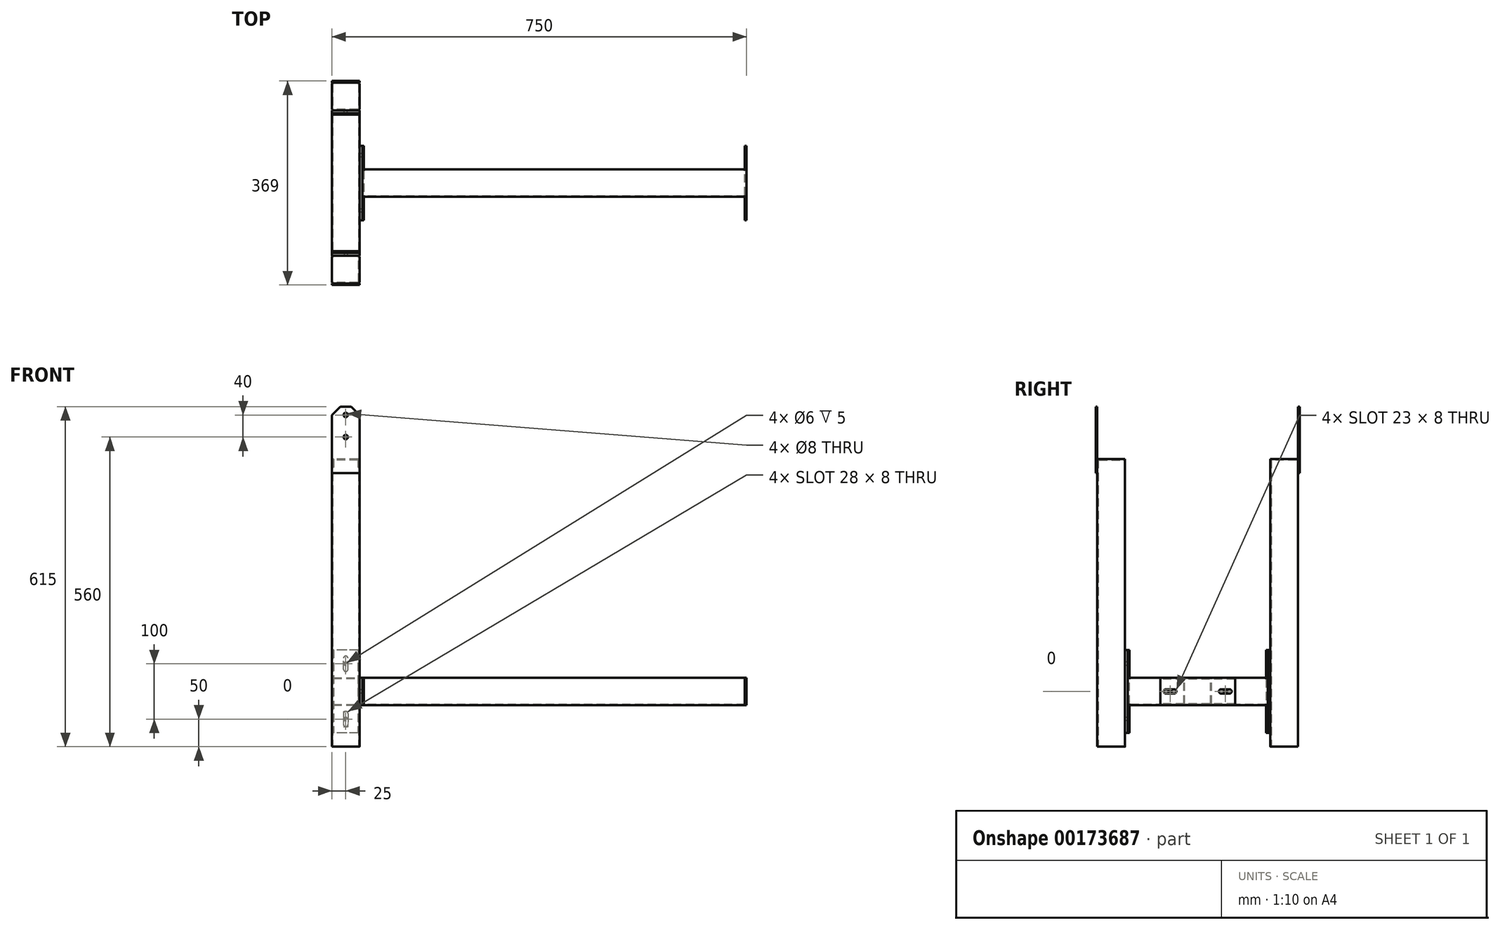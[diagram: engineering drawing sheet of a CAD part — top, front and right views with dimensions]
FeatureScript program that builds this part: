
annotation { "Feature Type Name" : "Feature", "Feature Type Description" : "" }
export const myFeature = defineFeature(function(context is Context, id is Id, definition is map)
    precondition{}
    {
        {
            var Q0;
            Q0=qCreatedBy(makeId("Top.planeOp"),FACE);
            var sketch = newSketch(context, id + "F0", { "sketchPlane" : qUnion([Q0])});
            skLineSegment(sketch, "E0.bottom", {"start": v(22, -25) * mm, "end": v(-22, -25) * mm});
            skLineSegment(sketch, "E0.top", {"start": v(22, 25) * mm, "end": v(-22, 25) * mm});
            skLineSegment(sketch, "E0.left", {"start": v(25, -22) * mm, "end": v(25, 22) * mm});
            skLineSegment(sketch, "E0.right", {"start": v(-25, -22) * mm, "end": v(-25, 22) * mm});
            skPoint(sketch, "E0.middle", {"position": v(0, 0) * mm});
            skPoint(sketch, "E1.visualSharp", {"position": v(-25, 25) * mm});
            skArc(sketch, "E1.filletArc", {"start": v(-22, 25) * mm, "mid": v(-24.12, 24.12) * mm, "end": v(-25, 22) * mm});
            skPoint(sketch, "E2.visualSharp", {"position": v(25, 25) * mm});
            skArc(sketch, "E2.filletArc", {"start": v(25, 22) * mm, "mid": v(24.12, 24.12) * mm, "end": v(22, 25) * mm});
            skPoint(sketch, "E3.visualSharp", {"position": v(25, -25) * mm});
            skArc(sketch, "E3.filletArc", {"start": v(22, -25) * mm, "mid": v(24.12, -24.12) * mm, "end": v(25, -22) * mm});
            skPoint(sketch, "E4.visualSharp", {"position": v(-25, -25) * mm});
            skArc(sketch, "E4.filletArc", {"start": v(-25, -22) * mm, "mid": v(-24.12, -24.12) * mm, "end": v(-22, -25) * mm});
            skArc(sketch, "E5.0", {"start": v(23.5, 22) * mm, "mid": v(23.06, 23.06) * mm, "end": v(22, 23.5) * mm});
            skLineSegment(sketch, "E5.1", {"start": v(23.5, -22) * mm, "end": v(23.5, 22) * mm});
            skLineSegment(sketch, "E5.2", {"start": v(22, 23.5) * mm, "end": v(-22, 23.5) * mm});
            skArc(sketch, "E5.3", {"start": v(22, -23.5) * mm, "mid": v(23.06, -23.06) * mm, "end": v(23.5, -22) * mm});
            skArc(sketch, "E5.4", {"start": v(-22, 23.5) * mm, "mid": v(-23.06, 23.06) * mm, "end": v(-23.5, 22) * mm});
            skLineSegment(sketch, "E5.5", {"start": v(-23.5, -22) * mm, "end": v(-23.5, 22) * mm});
            skArc(sketch, "E5.6", {"start": v(-23.5, -22) * mm, "mid": v(-23.06, -23.06) * mm, "end": v(-22, -23.5) * mm});
            skLineSegment(sketch, "E5.7", {"start": v(22, -23.5) * mm, "end": v(-22, -23.5) * mm});
            skSolve(sketch);
        }
        {
            var Q0;
            Q0=makeQuery(id+"F0.imprint","IMPRINT",FACE,{"disambiguationData":[TD([[makeQuery(id+"F0.imprint","IMPRINT",EDGE,{"derivedFrom":sQuery(id+"F0.wireOp",EDGE,"E0.bottom")}),-1.0]])]});
            extrude(context, id + "F1", {"entities" : qUnion([Q0]), "depth" : 520 * mm});
        }
        {
            var Q0;
            Q0=makeQuery(id+"F1.opExtrude","SWEPT_FACE",FACE,{"disambiguationData":[OSD([sQuery(id+"F0.wireOp",EDGE,"E0.top")])]});
            var sketch = newSketch(context, id + "F2", { "sketchPlane" : qUnion([Q0])});
            skLineSegment(sketch, "E6.bottom", {"start": v(-25, 175) * mm, "end": v(25, 175) * mm});
            skLineSegment(sketch, "E6.top", {"start": v(-25, 25) * mm, "end": v(25, 25) * mm});
            skLineSegment(sketch, "E6.left", {"start": v(-25, 175) * mm, "end": v(-25, 25) * mm});
            skLineSegment(sketch, "E6.right", {"start": v(25, 175) * mm, "end": v(25, 25) * mm});
            skCircle(sketch, "E7", {"center": v(0, 150) * mm, "radius": 3 * mm});
            skCircle(sketch, "E8", {"center": v(0, 50) * mm, "radius": 3 * mm});
            skLineSegment(sketch, "E9", {"start": v(25, 100) * mm, "end": v(-25, 100) * mm, "construction": true});
            skPoint(sketch, "E10.middle", {"position": v(0, 100) * mm});
            skLineSegment(sketch, "E11", {"start": v(0, 125) * mm, "end": v(0, 75) * mm, "construction": true});
            skLineSegment(sketch, "E12", {"start": v(-89.65, -125) * mm, "end": v(137.55, -125) * mm, "construction": true});
            skSolve(sketch);
        }
        {
            var Q0;
            Q0=qSketchRegion(id+"F2",true);
            extrude(context, id + "F3", {"entities" : qUnion([Q0]), "operationType" : NewBodyOperationType.ADD, "depth" : 5 * mm});
        }
        {
            var Q0;
            Q0=makeQuery(id+"F1.opExtrude","CAP_FACE",FACE,{"disambiguationData":[OSD([sQuery(id+"F0.wireOp",EDGE,"E0.bottom"),sQuery(id+"F0.wireOp",EDGE,"E0.top"),sQuery(id+"F0.wireOp",EDGE,"E0.left"),sQuery(id+"F0.wireOp",EDGE,"E0.right"),sQuery(id+"F0.wireOp",EDGE,"E1.filletArc"),sQuery(id+"F0.wireOp",EDGE,"E2.filletArc"),sQuery(id+"F0.wireOp",EDGE,"E3.filletArc"),sQuery(id+"F0.wireOp",EDGE,"E4.filletArc"),sQuery(id+"F0.wireOp",EDGE,"E5.0"),sQuery(id+"F0.wireOp",EDGE,"E5.1"),sQuery(id+"F0.wireOp",EDGE,"E5.2"),sQuery(id+"F0.wireOp",EDGE,"E5.3"),sQuery(id+"F0.wireOp",EDGE,"E5.4"),sQuery(id+"F0.wireOp",EDGE,"E5.5"),sQuery(id+"F0.wireOp",EDGE,"E5.6"),sQuery(id+"F0.wireOp",EDGE,"E5.7")])],"isStart":false});
            var sketch = newSketch(context, id + "F4", { "sketchPlane" : qUnion([Q0])});
            skLineSegment(sketch, "E13.0", {"start": v(-25, -22) * mm, "end": v(-25, 22) * mm});
            skArc(sketch, "E13.1", {"start": v(-25, -22) * mm, "mid": v(-24.12, -24.12) * mm, "end": v(-22, -25) * mm});
            skLineSegment(sketch, "E13.2", {"start": v(22, -25) * mm, "end": v(-22, -25) * mm});
            skArc(sketch, "E13.3", {"start": v(22, -25) * mm, "mid": v(24.12, -24.12) * mm, "end": v(25, -22) * mm});
            skLineSegment(sketch, "E13.4", {"start": v(25, -22) * mm, "end": v(25, 22) * mm});
            skArc(sketch, "E13.5", {"start": v(25, 22) * mm, "mid": v(24.12, 24.12) * mm, "end": v(22, 25) * mm});
            skLineSegment(sketch, "E13.6", {"start": v(22, 25) * mm, "end": v(-22, 25) * mm});
            skArc(sketch, "E13.7", {"start": v(-22, 25) * mm, "mid": v(-24.12, 24.12) * mm, "end": v(-25, 22) * mm});
            skSolve(sketch);
        }
        {
            var Q0;
            Q0=makeQuery(id+"F4.imprint","IMPRINT",FACE,{"disambiguationData":[TD([[makeQuery(id+"F4.imprint","IMPRINT",EDGE,{"derivedFrom":makeQuery(id+"F1.opExtrude","CAP_EDGE",EDGE,{"disambiguationData":[OSD([sQuery(id+"F0.wireOp",EDGE,"E5.0")])],"isStart":false})}),1.0]])]});
            extrude(context, id + "F5", {"entities" : qUnion([Q0]), "operationType" : NewBodyOperationType.ADD, "oppositeDirection" : true, "depth" : 1.5 * mm});
        }
        {
            var Q0;
            Q0=makeQuery(id+"F1.opExtrude","SWEPT_FACE",FACE,{"disambiguationData":[OSD([sQuery(id+"F0.wireOp",EDGE,"E0.bottom")])]});
            var sketch = newSketch(context, id + "F6", { "sketchPlane" : qUnion([Q0])});
            skLineSegment(sketch, "E14.bottom", {"start": v(-25, 615) * mm, "end": v(25, 615) * mm});
            skLineSegment(sketch, "E14.top", {"start": v(-25, 495) * mm, "end": v(25, 495) * mm});
            skLineSegment(sketch, "E14.left", {"start": v(-25, 615) * mm, "end": v(-25, 495) * mm});
            skLineSegment(sketch, "E14.right", {"start": v(25, 615) * mm, "end": v(25, 495) * mm});
            skCircle(sketch, "E15", {"center": v(0, 600) * mm, "radius": 4 * mm});
            skCircle(sketch, "E16", {"center": v(0, 560) * mm, "radius": 4 * mm});
            skSolve(sketch);
        }
        {
            var Q0;
            Q0=qSketchRegion(id+"F6",true);
            extrude(context, id + "F7", {"entities" : qUnion([Q0]), "operationType" : NewBodyOperationType.ADD, "depth" : 3 * mm});
        }
        {
            var Q0;
            Q0=makeQuery(id+"F7.opExtrude","SWEPT_EDGE",EDGE,{"disambiguationData":[OSD([sQuery(id+"F6.wireOp",EDGE,"E14.bottom"),sQuery(id+"F6.wireOp",EDGE,"E14.right")])]});
            var Q1;
            Q1=makeQuery(id+"F7.opExtrude","SWEPT_EDGE",EDGE,{"disambiguationData":[OSD([sQuery(id+"F6.wireOp",EDGE,"E14.bottom"),sQuery(id+"F6.wireOp",EDGE,"E14.left")])]});
            chamfer(context, id + "F8", {"entities" : qUnion([Q0, Q1]), "width" : 15 * mm, "tangentPropagation" : true});
        }
        {
            var Q0;
            Q0=makeQuery(id+"F7.opExtrude","CAP_FACE",FACE,{"disambiguationData":[OSD([sQuery(id+"F6.wireOp",EDGE,"E14.bottom"),sQuery(id+"F6.wireOp",EDGE,"E14.top"),sQuery(id+"F6.wireOp",EDGE,"E14.left"),sQuery(id+"F6.wireOp",EDGE,"E14.right"),sQuery(id+"F6.wireOp",EDGE,"E15"),sQuery(id+"F6.wireOp",EDGE,"E16")])],"isStart":true});
            cPlane(context, id + "F9", {"entities" : qUnion([Q0]), "cplaneType" : CPlaneType.OFFSET, "offset" : (363 / 2) * mm, "width" : 150 * mm, "height" : 150 * mm});
        }
        {
            var Q0;
            Q0=makeQuery(id+"F1.opExtrude","SWEPT_BODY",BODY,{"disambiguationData":[OSD([sQuery(id+"F0.wireOp",EDGE,"E0.bottom"),sQuery(id+"F0.wireOp",EDGE,"E0.top"),sQuery(id+"F0.wireOp",EDGE,"E0.left"),sQuery(id+"F0.wireOp",EDGE,"E0.right"),sQuery(id+"F0.wireOp",EDGE,"E1.filletArc"),sQuery(id+"F0.wireOp",EDGE,"E2.filletArc"),sQuery(id+"F0.wireOp",EDGE,"E3.filletArc"),sQuery(id+"F0.wireOp",EDGE,"E4.filletArc"),sQuery(id+"F0.wireOp",EDGE,"E5.0"),sQuery(id+"F0.wireOp",EDGE,"E5.1"),sQuery(id+"F0.wireOp",EDGE,"E5.2"),sQuery(id+"F0.wireOp",EDGE,"E5.3"),sQuery(id+"F0.wireOp",EDGE,"E5.4"),sQuery(id+"F0.wireOp",EDGE,"E5.5"),sQuery(id+"F0.wireOp",EDGE,"E5.6"),sQuery(id+"F0.wireOp",EDGE,"E5.7")])]});
            var Q1;
            Q1=qCreatedBy(id+"F9.planeOp",FACE);
            mirror(context, id + "F10", {"entities" : qUnion([Q0]), "mirrorPlane" : qUnion([Q1])});
        }
        {
            var Q0;
            Q0=makeQuery(id+"F3.opExtrude","CAP_FACE",FACE,{"disambiguationData":[OSD([sQuery(id+"F2.wireOp",EDGE,"E6.bottom"),sQuery(id+"F2.wireOp",EDGE,"E6.top"),sQuery(id+"F2.wireOp",EDGE,"E6.left"),sQuery(id+"F2.wireOp",EDGE,"E6.right"),sQuery(id+"F2.wireOp",EDGE,"E7"),sQuery(id+"F2.wireOp",EDGE,"E8")])],"isStart":false});
            var sketch = newSketch(context, id + "F11", { "sketchPlane" : qUnion([Q0])});
            skLineSegment(sketch, "E17.0", {"start": v(-25, 175) * mm, "end": v(25, 175) * mm});
            skLineSegment(sketch, "E17.1", {"start": v(25, 175) * mm, "end": v(25, 25) * mm});
            skLineSegment(sketch, "E17.2", {"start": v(-25, 175) * mm, "end": v(-25, 25) * mm});
            skLineSegment(sketch, "E17.3", {"start": v(-25, 25) * mm, "end": v(25, 25) * mm});
            skCircle(sketch, "E18.0", {"center": v(0, 150) * mm, "radius": 3 * mm, "construction": true});
            skCircle(sketch, "E18.1", {"center": v(0, 50) * mm, "radius": 3 * mm, "construction": true});
            skLineSegment(sketch, "E19.bottom", {"start": v(4, 140) * mm, "end": v(-4, 140) * mm, "construction": true});
            skLineSegment(sketch, "E19.top", {"start": v(4, 160) * mm, "end": v(-4, 160) * mm, "construction": true});
            skLineSegment(sketch, "E19.left", {"start": v(4, 140) * mm, "end": v(4, 160) * mm});
            skLineSegment(sketch, "E19.right", {"start": v(-4, 140) * mm, "end": v(-4, 160) * mm});
            skLineSegment(sketch, "E20.bottom", {"start": v(-4, 60) * mm, "end": v(4, 60) * mm, "construction": true});
            skLineSegment(sketch, "E20.top", {"start": v(-4, 40) * mm, "end": v(4, 40) * mm, "construction": true});
            skLineSegment(sketch, "E20.left", {"start": v(-4, 60) * mm, "end": v(-4, 40) * mm});
            skLineSegment(sketch, "E20.right", {"start": v(4, 60) * mm, "end": v(4, 40) * mm});
            skArc(sketch, "E21", {"start": v(4, 160) * mm, "mid": v(0, 164) * mm, "end": v(-4, 160) * mm});
            skArc(sketch, "E22", {"start": v(-4, 140) * mm, "mid": v(0, 136) * mm, "end": v(4, 140) * mm});
            skArc(sketch, "E23", {"start": v(4, 60) * mm, "mid": v(0, 64) * mm, "end": v(-4, 60) * mm});
            skArc(sketch, "E24", {"start": v(-4, 40) * mm, "mid": v(0, 36) * mm, "end": v(4, 40) * mm});
            skSolve(sketch);
        }
        {
            var Q0;
            Q0=qSketchRegion(id+"F11",true);
            extrude(context, id + "F12", {"entities" : qUnion([Q0]), "depth" : 3 * mm});
        }
        {
            var Q0;
            Q0=makeQuery(id+"F12.opExtrude","SWEPT_BODY",BODY,{"disambiguationData":[OSD([sQuery(id+"F11.wireOp",EDGE,"E17.0"),sQuery(id+"F11.wireOp",EDGE,"E17.1"),sQuery(id+"F11.wireOp",EDGE,"E17.2"),sQuery(id+"F11.wireOp",EDGE,"E17.3"),sQuery(id+"F11.wireOp",EDGE,"E19.left"),sQuery(id+"F11.wireOp",EDGE,"E19.right"),sQuery(id+"F11.wireOp",EDGE,"E20.left"),sQuery(id+"F11.wireOp",EDGE,"E20.right"),sQuery(id+"F11.wireOp",EDGE,"E21"),sQuery(id+"F11.wireOp",EDGE,"E22"),sQuery(id+"F11.wireOp",EDGE,"E23"),sQuery(id+"F11.wireOp",EDGE,"E24")])]});
            var Q1;
            Q1=qCreatedBy(id+"F9.planeOp",FACE);
            mirror(context, id + "F13", {"entities" : qUnion([Q0]), "mirrorPlane" : qUnion([Q1])});
        }
        {
            var Q0;
            Q0=makeQuery(id+"F12.opExtrude","CAP_FACE",FACE,{"disambiguationData":[OSD([sQuery(id+"F11.wireOp",EDGE,"E17.0"),sQuery(id+"F11.wireOp",EDGE,"E17.1"),sQuery(id+"F11.wireOp",EDGE,"E17.2"),sQuery(id+"F11.wireOp",EDGE,"E17.3"),sQuery(id+"F11.wireOp",EDGE,"E19.left"),sQuery(id+"F11.wireOp",EDGE,"E19.right"),sQuery(id+"F11.wireOp",EDGE,"E20.left"),sQuery(id+"F11.wireOp",EDGE,"E20.right"),sQuery(id+"F11.wireOp",EDGE,"E21"),sQuery(id+"F11.wireOp",EDGE,"E22"),sQuery(id+"F11.wireOp",EDGE,"E23"),sQuery(id+"F11.wireOp",EDGE,"E24")])],"isStart":false});
            var sketch = newSketch(context, id + "F14", { "sketchPlane" : qUnion([Q0])});
            skLineSegment(sketch, "E25", {"start": v(-25, 100) * mm, "end": v(25, 100) * mm, "construction": true});
            skLineSegment(sketch, "E26.bottom", {"start": v(22, 75) * mm, "end": v(-22, 75) * mm});
            skLineSegment(sketch, "E26.top", {"start": v(22, 125) * mm, "end": v(-22, 125) * mm});
            skLineSegment(sketch, "E26.left", {"start": v(25, 78) * mm, "end": v(25, 122) * mm});
            skLineSegment(sketch, "E26.right", {"start": v(-25, 78) * mm, "end": v(-25, 122) * mm});
            skPoint(sketch, "E26.middle", {"position": v(0, 100) * mm});
            skPoint(sketch, "E27.visualSharp", {"position": v(-25, 125) * mm});
            skArc(sketch, "E27.filletArc", {"start": v(-22, 125) * mm, "mid": v(-24.12, 124.12) * mm, "end": v(-25, 122) * mm});
            skPoint(sketch, "E28.visualSharp", {"position": v(25, 125) * mm});
            skArc(sketch, "E28.filletArc", {"start": v(25, 122) * mm, "mid": v(24.12, 124.12) * mm, "end": v(22, 125) * mm});
            skPoint(sketch, "E29.visualSharp", {"position": v(25, 75) * mm});
            skArc(sketch, "E29.filletArc", {"start": v(22, 75) * mm, "mid": v(24.12, 75.88) * mm, "end": v(25, 78) * mm});
            skPoint(sketch, "E30.visualSharp", {"position": v(-25, 75) * mm});
            skArc(sketch, "E30.filletArc", {"start": v(-25, 78) * mm, "mid": v(-24.12, 75.88) * mm, "end": v(-22, 75) * mm});
            skArc(sketch, "E31.0", {"start": v(23.5, 122) * mm, "mid": v(23.06, 123.06) * mm, "end": v(22, 123.5) * mm});
            skLineSegment(sketch, "E31.1", {"start": v(23.5, 78) * mm, "end": v(23.5, 122) * mm});
            skLineSegment(sketch, "E31.2", {"start": v(22, 123.5) * mm, "end": v(-22, 123.5) * mm});
            skArc(sketch, "E31.3", {"start": v(22, 76.5) * mm, "mid": v(23.06, 76.94) * mm, "end": v(23.5, 78) * mm});
            skArc(sketch, "E31.4", {"start": v(-22, 123.5) * mm, "mid": v(-23.06, 123.06) * mm, "end": v(-23.5, 122) * mm});
            skLineSegment(sketch, "E31.5", {"start": v(-23.5, 78) * mm, "end": v(-23.5, 122) * mm});
            skArc(sketch, "E31.6", {"start": v(-23.5, 78) * mm, "mid": v(-23.06, 76.94) * mm, "end": v(-22, 76.5) * mm});
            skLineSegment(sketch, "E31.7", {"start": v(22, 76.5) * mm, "end": v(-22, 76.5) * mm});
            skSolve(sketch);
        }
        {
            var Q0;
            Q0=qSketchRegion(id+"F14",true);
            extrude(context, id + "F15", {"entities" : qUnion([Q0]), "operationType" : NewBodyOperationType.ADD, "endBound" : BoundingType.UP_TO_NEXT, "depth" : 25 * mm});
        }
        {
            var Q0;
            Q0=makeQuery(id+"F1.opExtrude","SWEPT_FACE",FACE,{"disambiguationData":[OSD([sQuery(id+"F0.wireOp",EDGE,"E0.left")])]});
            cPlane(context, id + "F16", {"entities" : qUnion([Q0]), "cplaneType" : CPlaneType.OFFSET, "offset" : 352.5 * mm, "width" : 150 * mm, "height" : 150 * mm});
        }
        {
            var Q0;
            {var subQ0=makeQuery(id+"F12.opExtrude","SWEPT_FACE",FACE,{"disambiguationData":[OSD([sQuery(id+"F11.wireOp",EDGE,"E17.2")])]});Q0=makeQuery(id+"F15.boolean.opBoolean","MERGE",FACE,{"derivedFrom":[subQ0,makeQuery(id+"F13.opPattern","COPY",FACE,{"derivedFrom":subQ0,"instanceName":"1"}),makeQuery(id+"F15.opExtrude","SWEPT_FACE",FACE,{"disambiguationData":[OSD([sQuery(id+"F14.wireOp",EDGE,"E26.right")])]})]});}
            var sketch = newSketch(context, id + "F17", { "sketchPlane" : qUnion([Q0])});
            skLineSegment(sketch, "E32.bottom", {"start": v(89, 125) * mm, "end": v(224, 125) * mm});
            skLineSegment(sketch, "E32.top", {"start": v(89, 75) * mm, "end": v(224, 75) * mm});
            skLineSegment(sketch, "E32.left", {"start": v(89, 125) * mm, "end": v(89, 75) * mm});
            skLineSegment(sketch, "E32.right", {"start": v(224, 125) * mm, "end": v(224, 75) * mm});
            skLineSegment(sketch, "E33", {"start": v(224, 100) * mm, "end": v(89, 100) * mm, "construction": true});
            skPoint(sketch, "E34.middle", {"position": v(156.5, 100) * mm});
            skLineSegment(sketch, "E35", {"start": v(156.5, 122) * mm, "end": v(156.5, 78) * mm, "construction": true});
            skCircle(sketch, "E36", {"center": v(106.5, 100) * mm, "radius": 3 * mm});
            skCircle(sketch, "E37.MirrorC", {"center": v(206.5, 100) * mm, "radius": 3 * mm});
            skSolve(sketch);
        }
        {
            var Q0;
            Q0=qSketchRegion(id+"F17",true);
            extrude(context, id + "F18", {"entities" : qUnion([Q0]), "operationType" : NewBodyOperationType.ADD, "depth" : 5 * mm});
        }
        {
            var Q0;
            Q0=makeQuery(id+"F18.opExtrude","CAP_FACE",FACE,{"disambiguationData":[OSD([sQuery(id+"F17.wireOp",EDGE,"E32.bottom"),sQuery(id+"F17.wireOp",EDGE,"E32.top"),sQuery(id+"F17.wireOp",EDGE,"E32.left"),sQuery(id+"F17.wireOp",EDGE,"E32.right"),sQuery(id+"F17.wireOp",EDGE,"E36"),sQuery(id+"F17.wireOp",EDGE,"E37.MirrorC")])],"isStart":false});
            var sketch = newSketch(context, id + "F19", { "sketchPlane" : qUnion([Q0])});
            skLineSegment(sketch, "E38.0", {"start": v(89, 125) * mm, "end": v(224, 125) * mm});
            skLineSegment(sketch, "E38.1", {"start": v(89, 125) * mm, "end": v(89, 75) * mm});
            skLineSegment(sketch, "E38.2", {"start": v(89, 75) * mm, "end": v(224, 75) * mm});
            skLineSegment(sketch, "E38.3", {"start": v(224, 125) * mm, "end": v(224, 75) * mm});
            skCircle(sketch, "E38.4", {"center": v(206.5, 100) * mm, "radius": 3 * mm, "construction": true});
            skCircle(sketch, "E38.5", {"center": v(106.5, 100) * mm, "radius": 3 * mm, "construction": true});
            skCircle(sketch, "E39", {"center": v(106.5, 100) * mm, "radius": 4 * mm});
            skCircle(sketch, "E40", {"center": v(206.5, 100) * mm, "radius": 4 * mm});
            skSolve(sketch);
        }
        {
            var Q0;
            Q0=qSketchRegion(id+"F19",true);
            extrude(context, id + "F20", {"entities" : qUnion([Q0]), "depth" : 3 * mm});
        }
        {
            var Q0;
            Q0=makeQuery(id+"F20.opExtrude","SWEPT_BODY",BODY,{"disambiguationData":[OSD([sQuery(id+"F19.wireOp",EDGE,"E38.0"),sQuery(id+"F19.wireOp",EDGE,"E38.1"),sQuery(id+"F19.wireOp",EDGE,"E38.2"),sQuery(id+"F19.wireOp",EDGE,"E38.3"),sQuery(id+"F19.wireOp",EDGE,"E39"),sQuery(id+"F19.wireOp",EDGE,"E40")])]});
            var Q1;
            Q1=qCreatedBy(id+"F16.planeOp",FACE);
            mirror(context, id + "F21", {"entities" : qUnion([Q0]), "mirrorPlane" : qUnion([Q1])});
        }
        {
            var Q0;
            Q0=makeQuery(id+"F20.opExtrude","CAP_FACE",FACE,{"disambiguationData":[OSD([sQuery(id+"F19.wireOp",EDGE,"E38.0"),sQuery(id+"F19.wireOp",EDGE,"E38.1"),sQuery(id+"F19.wireOp",EDGE,"E38.2"),sQuery(id+"F19.wireOp",EDGE,"E38.3"),sQuery(id+"F19.wireOp",EDGE,"E39"),sQuery(id+"F19.wireOp",EDGE,"E40")])],"isStart":false});
            var sketch = newSketch(context, id + "F22", { "sketchPlane" : qUnion([Q0])});
            skLineSegment(sketch, "E41", {"start": v(139.88, 100) * mm, "end": v(173.12, 100) * mm, "construction": true});
            skLineSegment(sketch, "E42.bottom", {"start": v(178.5, 75) * mm, "end": v(134.5, 75) * mm});
            skLineSegment(sketch, "E42.top", {"start": v(178.5, 125) * mm, "end": v(134.5, 125) * mm});
            skLineSegment(sketch, "E42.left", {"start": v(181.5, 78) * mm, "end": v(181.5, 122) * mm});
            skLineSegment(sketch, "E42.right", {"start": v(131.5, 78) * mm, "end": v(131.5, 122) * mm});
            skPoint(sketch, "E42.middle", {"position": v(156.5, 100) * mm});
            skPoint(sketch, "E43.visualSharp", {"position": v(131.5, 125) * mm});
            skArc(sketch, "E43.filletArc", {"start": v(134.5, 125) * mm, "mid": v(132.38, 124.12) * mm, "end": v(131.5, 122) * mm});
            skPoint(sketch, "E44.visualSharp", {"position": v(181.5, 125) * mm});
            skArc(sketch, "E44.filletArc", {"start": v(181.5, 122) * mm, "mid": v(180.62, 124.12) * mm, "end": v(178.5, 125) * mm});
            skPoint(sketch, "E45.visualSharp", {"position": v(181.5, 75) * mm});
            skArc(sketch, "E45.filletArc", {"start": v(178.5, 75) * mm, "mid": v(180.62, 75.88) * mm, "end": v(181.5, 78) * mm});
            skPoint(sketch, "E46.visualSharp", {"position": v(131.5, 75) * mm});
            skArc(sketch, "E46.filletArc", {"start": v(131.5, 78) * mm, "mid": v(132.38, 75.88) * mm, "end": v(134.5, 75) * mm});
            skArc(sketch, "E47.0", {"start": v(180, 122) * mm, "mid": v(179.56, 123.06) * mm, "end": v(178.5, 123.5) * mm});
            skLineSegment(sketch, "E47.1", {"start": v(180, 78) * mm, "end": v(180, 122) * mm});
            skLineSegment(sketch, "E47.2", {"start": v(178.5, 123.5) * mm, "end": v(134.5, 123.5) * mm});
            skArc(sketch, "E47.3", {"start": v(178.5, 76.5) * mm, "mid": v(179.56, 76.94) * mm, "end": v(180, 78) * mm});
            skArc(sketch, "E47.4", {"start": v(134.5, 123.5) * mm, "mid": v(133.44, 123.06) * mm, "end": v(133, 122) * mm});
            skLineSegment(sketch, "E47.5", {"start": v(133, 78) * mm, "end": v(133, 122) * mm});
            skArc(sketch, "E47.6", {"start": v(133, 78) * mm, "mid": v(133.44, 76.94) * mm, "end": v(134.5, 76.5) * mm});
            skLineSegment(sketch, "E47.7", {"start": v(178.5, 76.5) * mm, "end": v(134.5, 76.5) * mm});
            skLineSegment(sketch, "E48", {"start": v(156.5, 100) * mm, "end": v(156.5, 125) * mm, "construction": true});
            skSolve(sketch);
        }
        {
            var Q0;
            Q0=qSketchRegion(id+"F22",true);
            extrude(context, id + "F23", {"entities" : qUnion([Q0]), "operationType" : NewBodyOperationType.ADD, "endBound" : BoundingType.UP_TO_NEXT, "depth" : 25 * mm});
        }
        {
            var Q0;
            Q0=makeQuery(id+"F21.opPattern","COPY",FACE,{"derivedFrom":makeQuery(id+"F20.opExtrude","CAP_FACE",FACE,{"disambiguationData":[OSD([sQuery(id+"F19.wireOp",EDGE,"E38.0"),sQuery(id+"F19.wireOp",EDGE,"E38.1"),sQuery(id+"F19.wireOp",EDGE,"E38.2"),sQuery(id+"F19.wireOp",EDGE,"E38.3"),sQuery(id+"F19.wireOp",EDGE,"E39"),sQuery(id+"F19.wireOp",EDGE,"E40")])],"isStart":true}),"instanceName":"1"});
            var sketch = newSketch(context, id + "F24", { "sketchPlane" : qUnion([Q0])});
            skLineSegment(sketch, "E49.bottom", {"start": v(114, 96) * mm, "end": v(99, 96) * mm});
            skLineSegment(sketch, "E49.top", {"start": v(114, 104) * mm, "end": v(99, 104) * mm});
            skLineSegment(sketch, "E49.left", {"start": v(114, 96) * mm, "end": v(114, 104) * mm, "construction": true});
            skLineSegment(sketch, "E49.right", {"start": v(99, 96) * mm, "end": v(99, 104) * mm, "construction": true});
            skPoint(sketch, "E49.middle", {"position": v(106.5, 100) * mm});
            skLineSegment(sketch, "E50", {"start": v(156.5, 125) * mm, "end": v(156.5, 75) * mm, "construction": true});
            skArc(sketch, "E51", {"start": v(99, 104) * mm, "mid": v(95, 100) * mm, "end": v(99, 96) * mm});
            skArc(sketch, "E52", {"start": v(114, 96) * mm, "mid": v(118, 100) * mm, "end": v(114, 104) * mm});
            skArc(sketch, "E53.MirrorCS", {"start": v(199, 96) * mm, "mid": v(195, 100) * mm, "end": v(199, 104) * mm});
            skLineSegment(sketch, "E54.MirrorCS", {"start": v(199, 104) * mm, "end": v(214, 104) * mm});
            skArc(sketch, "E55.MirrorCS", {"start": v(214, 104) * mm, "mid": v(218, 100) * mm, "end": v(214, 96) * mm});
            skLineSegment(sketch, "E56.MirrorCS", {"start": v(199, 96) * mm, "end": v(214, 96) * mm});
            skSolve(sketch);
        }
        {
            var Q0;
            Q0=qSketchRegion(id+"F24",true);
            extrude(context, id + "F25", {"entities" : qUnion([Q0]), "operationType" : NewBodyOperationType.REMOVE, "endBound" : BoundingType.UP_TO_NEXT, "oppositeDirection" : true, "depth" : 25 * mm});
        }
    });
